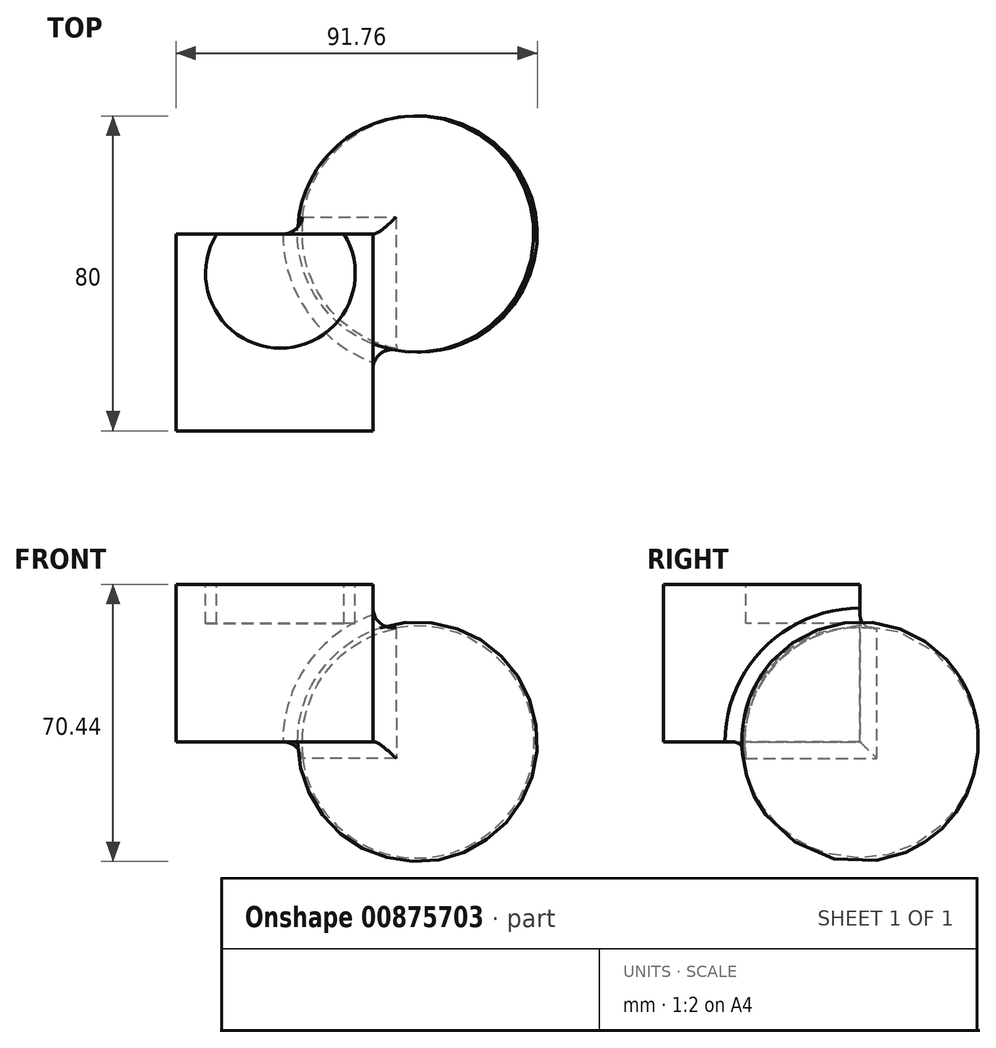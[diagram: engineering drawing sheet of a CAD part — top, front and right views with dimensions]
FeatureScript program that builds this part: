
annotation { "Feature Type Name" : "Feature", "Feature Type Description" : "" }
export const myFeature = defineFeature(function(context is Context, id is Id, definition is map)
    precondition{}
    {
        {
            var Q0;
            Q0=qCreatedBy(makeId("Front.planeOp"),FACE);
            var sketch = newSketch(context, id + "F0", { "sketchPlane" : qUnion([Q0])});
            skLineSegment(sketch, "E0.bottom", {"start": v(-11.76, 0) * mm, "end": v(-61.76, 0) * mm});
            skLineSegment(sketch, "E0.top", {"start": v(-11.76, 40) * mm, "end": v(-61.76, 40) * mm});
            skLineSegment(sketch, "E0.left", {"start": v(-11.76, 0) * mm, "end": v(-11.76, 40) * mm});
            skLineSegment(sketch, "E0.right", {"start": v(-61.76, 0) * mm, "end": v(-61.76, 40) * mm});
            skSolve(sketch);
        }
        {
            var Q0;
            Q0=qCreatedBy(makeId("Top.planeOp"),FACE);
            var sketch = newSketch(context, id + "F1", { "sketchPlane" : qUnion([Q0])});
            skArc(sketch, "E1", {"start": v(-0.89, 29.99) * mm, "mid": v(-30, -0.44) * mm, "end": v(0, -30) * mm});
            skLineSegment(sketch, "E2", {"start": v(-0.89, 29.99) * mm, "end": v(0, -30) * mm});
            skSolve(sketch);
        }
        {
            var Q0;
            Q0=makeQuery(id+"F1.imprint","IMPRINT",FACE,{"disambiguationData":[TD([[makeQuery(id+"F1.imprint","IMPRINT",EDGE,{"derivedFrom":sQuery(id+"F1.wireOp",EDGE,"E1")}),1.0]])]});
            var Q1;
            Q1=sQuery(id+"F1.wireOp",EDGE,"E2");
            revolve(context, id + "F2", {"surfaceOperationType" : NewSurfaceOperationType.NEW, "entities" : qUnion([Q0]), "axis" : qUnion([Q1]), "revolveType" : RevolveType.FULL});
        }
        {
            var Q0;
            Q0=makeQuery(id+"F0.imprint","IMPRINT",FACE,{"disambiguationData":[TD([[makeQuery(id+"F0.imprint","IMPRINT",EDGE,{"derivedFrom":sQuery(id+"F0.wireOp",EDGE,"E0.bottom")}),-1.0]])]});
            extrude(context, id + "F3", {"entities" : qUnion([Q0]), "operationType" : NewBodyOperationType.ADD, "depth" : 50 * mm, "offsetDistance" : 25 * mm});
        }
        {
            var Q0;
            Q0=makeQuery(id+"F3.boolean.opBoolean","INTERSECT",EDGE,{"derivedFrom":[makeQuery(id+"F2.opRevolve","SWEPT_FACE",FACE,{"disambiguationData":[OSD([sQuery(id+"F1.wireOp",EDGE,"E1")])]}),makeQuery(id+"F3.opExtrude","SWEPT_FACE",FACE,{"disambiguationData":[OSD([sQuery(id+"F0.wireOp",EDGE,"E0.left")])]})]});
            fillet(context, id + "F4", {"entities" : qUnion([Q0]), "radius" : 5 * mm, "tangentPropagation" : true, "allowEdgeOverflow" : false});
        }
        {
            var Q0;
            Q0=makeQuery(id+"F3.boolean.opBoolean","INTERSECT",EDGE,{"derivedFrom":[makeQuery(id+"F2.opRevolve","SWEPT_FACE",FACE,{"disambiguationData":[OSD([sQuery(id+"F1.wireOp",EDGE,"E1")])]}),makeQuery(id+"F3.opExtrude","SWEPT_FACE",FACE,{"disambiguationData":[OSD([sQuery(id+"F0.wireOp",EDGE,"E0.bottom")])]})]});
            fillet(context, id + "F5", {"entities" : qUnion([Q0]), "radius" : 5 * mm, "tangentPropagation" : true, "allowEdgeOverflow" : false});
        }
        {
            var Q0;
            Q0=makeQuery(id+"F3.boolean.opBoolean","INTERSECT",EDGE,{"derivedFrom":[makeQuery(id+"F2.opRevolve","SWEPT_FACE",FACE,{"disambiguationData":[OSD([sQuery(id+"F1.wireOp",EDGE,"E1")])]}),makeQuery(id+"F3.opExtrude","CAP_FACE",FACE,{"disambiguationData":[OSD([sQuery(id+"F0.wireOp",EDGE,"E0.bottom"),sQuery(id+"F0.wireOp",EDGE,"E0.top"),sQuery(id+"F0.wireOp",EDGE,"E0.left"),sQuery(id+"F0.wireOp",EDGE,"E0.right")])],"isStart":true})]});
            fillet(context, id + "F6", {"entities" : qUnion([Q0]), "radius" : 5 * mm, "tangentPropagation" : true, "allowEdgeOverflow" : false});
        }
        {
            var Q0;
            Q0=makeQuery(id+"F3.opExtrude","SWEPT_FACE",FACE,{"disambiguationData":[OSD([sQuery(id+"F0.wireOp",EDGE,"E0.top")])]});
            var sketch = newSketch(context, id + "F7", { "sketchPlane" : qUnion([Q0])});
            skCircle(sketch, "E3", {"center": v(-35.25, -10) * mm, "radius": 19 * mm});
            skSolve(sketch);
        }
        {
            var Q0;
            Q0 = qSketchRegion(id + "F7", true);
            extrude(context, id + "F8", {"entities" : qUnion([Q0]), "operationType" : NewBodyOperationType.REMOVE, "oppositeDirection" : true, "depth" : 10 * mm, "offsetDistance" : 25 * mm});
        }
    });
